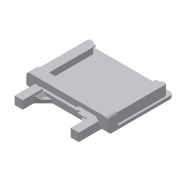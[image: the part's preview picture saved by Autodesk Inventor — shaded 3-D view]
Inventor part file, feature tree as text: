
AUTODESK INVENTOR PART (.ipt)
format: ipt  version: 2013 (Build 170138000, 138)  size: 270,336 bytes
history: native  units: mm
features: extrude x10, sketch x10, chamfer x8, fillet x5, projected_geometry x1
ambient origin geometry x8: Origin, YZ Plane, XZ Plane, XY Plane, X Axis, Y Axis, Z Axis, Center Point
feature tree (34):
  extrude  "Extrusion2"  Depth=65.0mm
  extrude  "Extrusion4"  Depth=1.85mm
  extrude  "Extrusion5"  Depth=10.0mm
  chamfer  "Fase3"  Distance=20.0mm
  chamfer  "Fase4"  Distance=9.0mm Angle=45.0deg
  chamfer  "Fase5"  Distance=9.0mm Angle=45.0deg
  extrude  "Extrusion6"  Depth=3.0mm TaperAngle=45.0deg
  extrude  "Extrusion7"  Depth=10.0mm
  chamfer  "Fase6"  Distance=7.5mm
  fillet  "Rundung13"  Radius=4.0mm
  chamfer  "Fase11"  Distance=3.0mm
  chamfer  "Fase12"  Distance=2.9999mm
  extrude  "Extrusion9"  Depth=2.9999mm
  extrude  "Extrusion11"  Depth=50.0mm
  extrude  "Extrusion12"  Depth=2.0mm
  fillet  "Rundung16"  Radius=2.0mm
  fillet  "Rundung17"  Radius=1.0mm
  extrude  "Extrusion13"  Depth=4.0mm TaperAngle=0.0deg
  fillet  "Rundung18"  Radius=1.0mm
  extrude  "Extrusion15"  Depth=4.0mm TaperAngle=0.0deg
  fillet  "Rundung19"  Radius=1.0mm
  chamfer  "Fase13"  Distance=4.0mm
  chamfer  "Fase14"  Distance=1.0mm
  sketch  "Skizze1"  dims[d0=80.0mm d1=65.0mm]
  sketch  "Skizze3"  dims[d32=3.0mm d33=0.0mm]
  projected_geometry  "Projizierte Kontur1"
  sketch  "Skizze5"  dims[d94=5.0mm d95=50.0mm d96=2.0mm d97=5.0mm d98=50.0mm d99=2.0mm d100=66.3mm d101=1.85mm]
  sketch  "Skizze6"  dims[d102=10.0mm d103=0.0mm d104=10.0mm]
  sketch  "Skizze7"  dims[d105=8.0mm]
  sketch  "Skizze9"  dims[d108=63.0mm]
  sketch  "Skizze11"  dims[d109=8.5mm d110=20.0mm d111=0.0mm]
  sketch  "Skizze12"  dims[d112=8.0mm d121=9.0mm d122=7.0mm d123=45.0deg d124=9.0mm d125=7.0mm d126=45.0deg]
  sketch  "Skizze13"  dims[d127=3.0mm d128=7.0mm d129=45.0deg d130=3.0mm d131=7.0mm d132=45.0deg]
  sketch  "Skizze15"  dims[d146=10.0mm d147=10.0mm d149=7.5mm d150=0.0mm d151=4.0mm d152=0.0mm d153=3.0mm d154=2.9999mm d155=7.0mm d156=6.981317mm d157=2.9999mm d158=7.0mm d159=6.981317mm d162=50.0mm d163=2.0mm d164=2.0mm d165=0.0mm d172=1.0mm d173=4.0mm d174=0.0mm d175=1.0mm d176=4.0mm d177=0.0mm d178=1.0mm d181=4.0mm d182=1.0mm d183=0.0mm d187=1.0mm d189=40.0mm d190=2.0mm d191=10.0mm d192=2.0mm d193=0.0mm d194=1.0mm d195=2.9999mm d196=7.0mm d197=6.981317mm d198=2.9999mm d199=7.0mm d200=6.981317mm d4=1.0mm d5=1.0mm]
